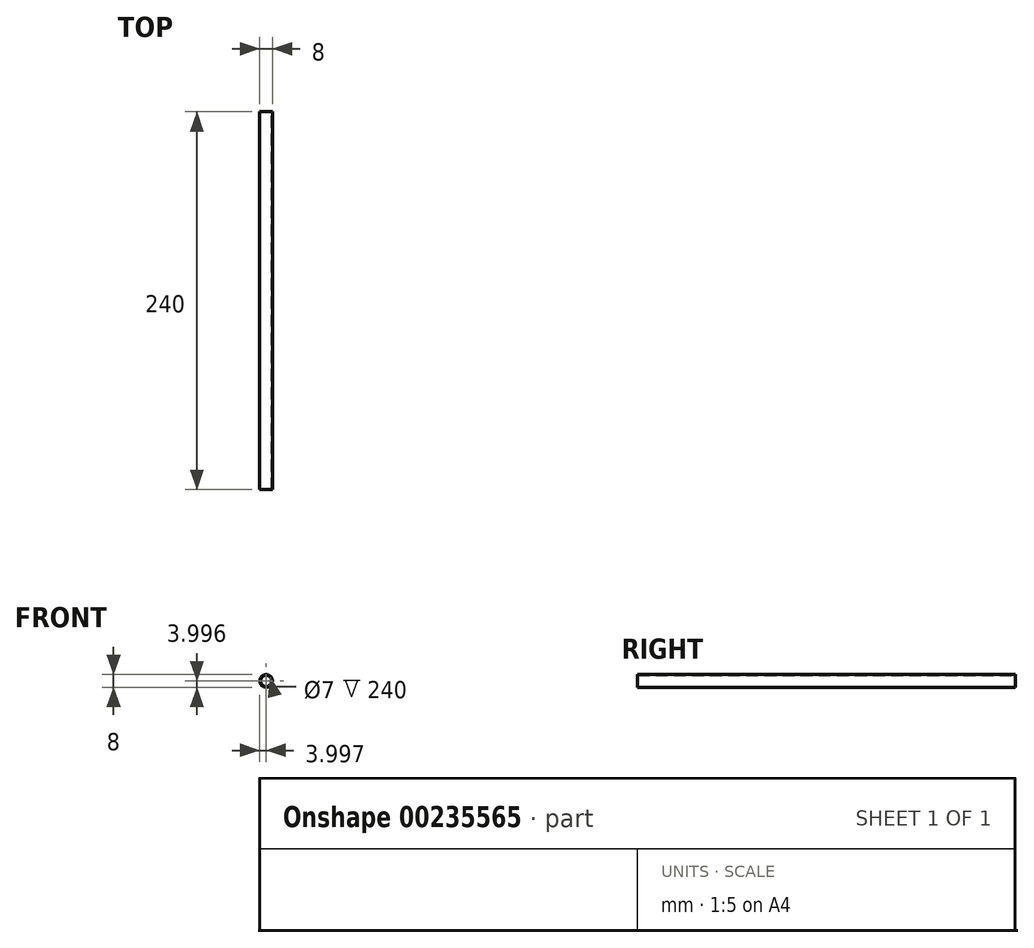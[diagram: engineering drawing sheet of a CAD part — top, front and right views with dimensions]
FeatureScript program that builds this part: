
annotation { "Feature Type Name" : "Feature", "Feature Type Description" : "" }
export const myFeature = defineFeature(function(context is Context, id is Id, definition is map)
    precondition{}
    {
        {
            var Q0;
            Q0=qCreatedBy(makeId("Front.planeOp"),FACE);
            var sketch = newSketch(context, id + "F0", { "sketchPlane" : qUnion([Q0])});
            skCircle(sketch, "E0", {"center": v(-22.95, 38.03) * mm, "radius": 4 * mm});
            skCircle(sketch, "E1", {"center": v(-22.95, 38.03) * mm, "radius": 3.5 * mm});
            skSolve(sketch);
        }
        {
            var Q0;
            Q0=qSketchRegion(id+"F0",true);
            extrude(context, id + "F1", {"entities" : qUnion([Q0]), "depth" : 240 * mm});
        }
    });
